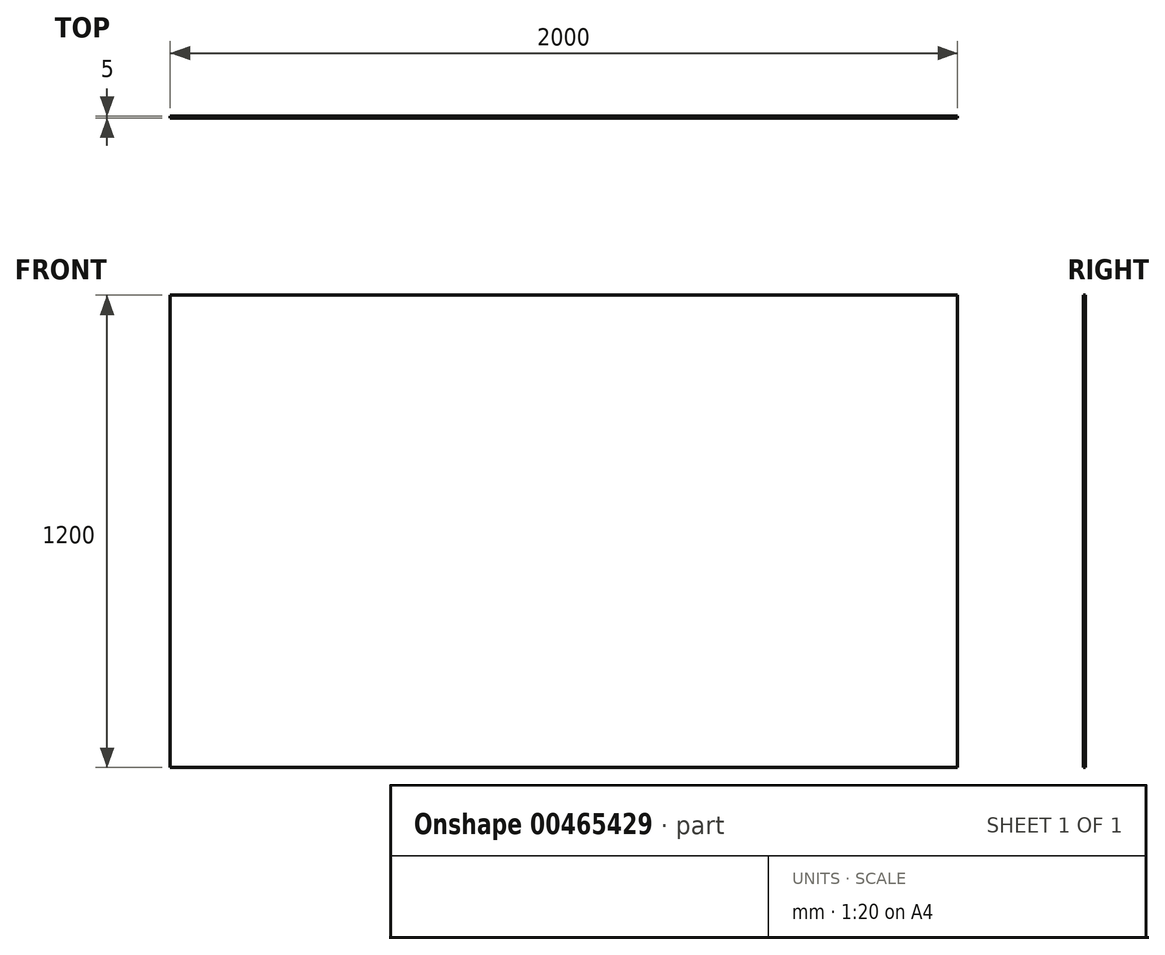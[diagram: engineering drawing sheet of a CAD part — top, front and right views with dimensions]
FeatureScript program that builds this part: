
annotation { "Feature Type Name" : "Feature", "Feature Type Description" : "" }
export const myFeature = defineFeature(function(context is Context, id is Id, definition is map)
    precondition{}
    {
        {
            var Q0;
            Q0=qCreatedBy(makeId("Front.planeOp"),FACE);
            var sketch = newSketch(context, id + "F0", { "sketchPlane" : qUnion([Q0])});
            skLineSegment(sketch, "E0.bottom", {"start": v(1000, 600) * mm, "end": v(-1000, 600) * mm});
            skLineSegment(sketch, "E0.top", {"start": v(1000, -600) * mm, "end": v(-1000, -600) * mm});
            skLineSegment(sketch, "E0.left", {"start": v(1000, 600) * mm, "end": v(1000, -600) * mm});
            skLineSegment(sketch, "E0.right", {"start": v(-1000, 600) * mm, "end": v(-1000, -600) * mm});
            skPoint(sketch, "E0.middle", {"position": v(0, 0) * mm});
            skSolve(sketch);
        }
        {
            var Q0;
            Q0 = qSketchRegion(id + "F0", true);
            extrude(context, id + "F1", {"entities" : qUnion([Q0]), "depth" : 5 * mm});
        }
    });
